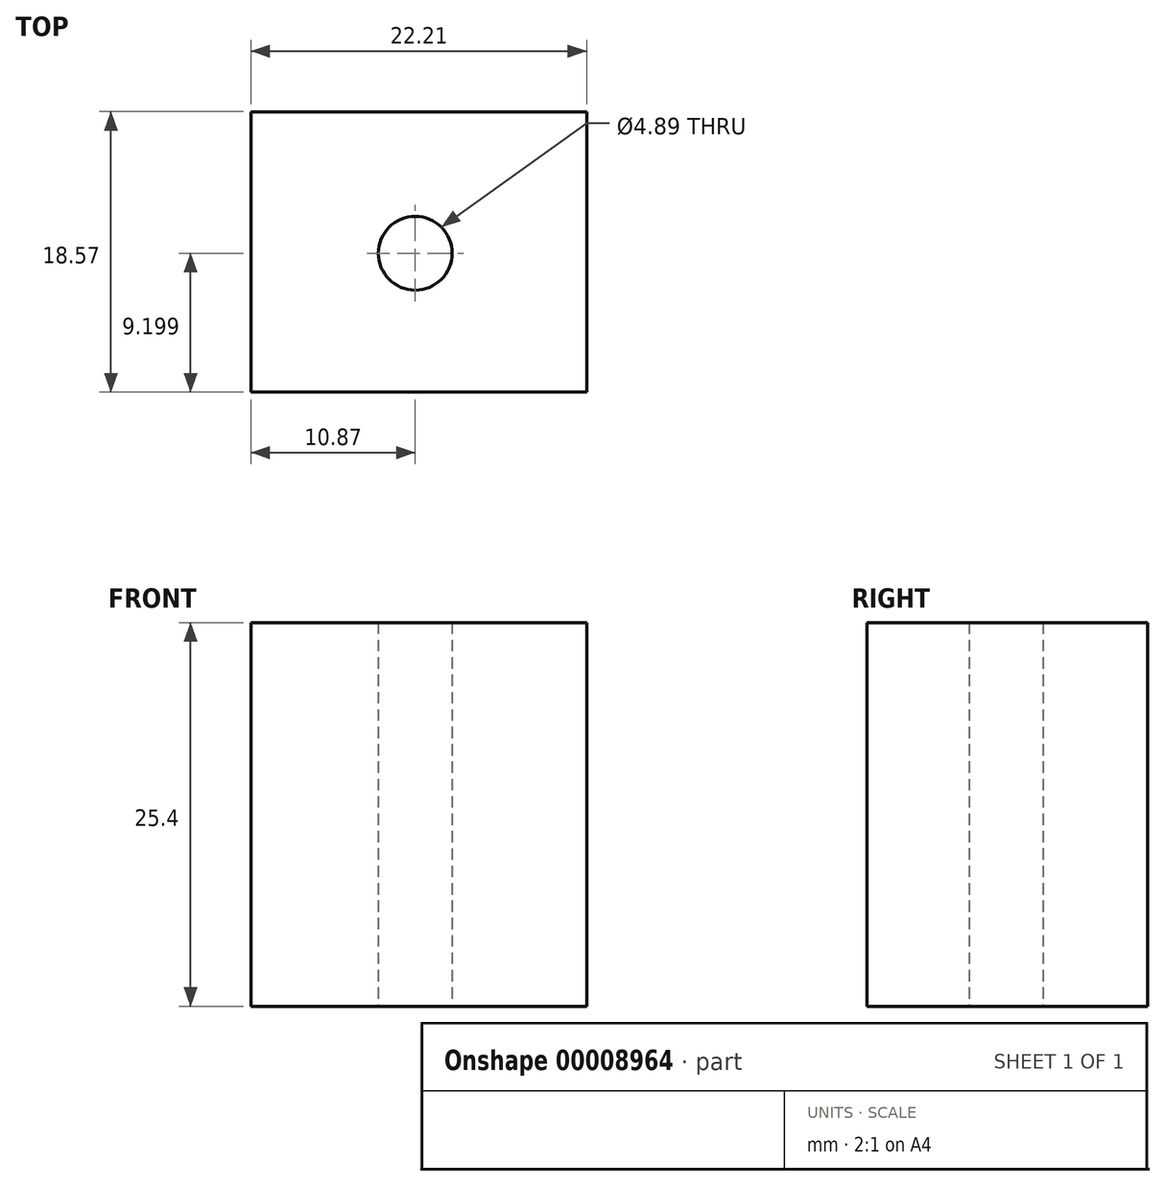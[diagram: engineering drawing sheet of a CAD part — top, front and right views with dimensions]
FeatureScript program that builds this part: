
annotation { "Feature Type Name" : "Feature", "Feature Type Description" : "" }
export const myFeature = defineFeature(function(context is Context, id is Id, definition is map)
    precondition{}
    {
        {
            var Q0;
            Q0=qCreatedBy(makeId("Top.planeOp"),FACE);
            var sketch = newSketch(context, id + "F0", { "sketchPlane" : qUnion([Q0])});
            skLineSegment(sketch, "E0.bottom", {"start": v(-58.65, -30.36) * mm, "end": v(-36.44, -30.36) * mm});
            skLineSegment(sketch, "E0.top", {"start": v(-58.65, -48.93) * mm, "end": v(-36.44, -48.93) * mm});
            skLineSegment(sketch, "E0.left", {"start": v(-58.65, -30.36) * mm, "end": v(-58.65, -48.93) * mm});
            skLineSegment(sketch, "E0.right", {"start": v(-36.44, -30.36) * mm, "end": v(-36.44, -48.93) * mm});
            skSolve(sketch);
        }
        {
            var Q0;
            Q0=makeQuery(id+"F0.imprint","IMPRINT",FACE,{"disambiguationData":[TD([[makeQuery(id+"F0.imprint","IMPRINT",EDGE,{"derivedFrom":sQuery(id+"F0.wireOp",EDGE,"E0.bottom")}),-1.0]])]});
            extrude(context, id + "F1", {"entities" : qUnion([Q0]), "depth" : 25.4 * mm});
        }
        {
            var Q0;
            Q0=qCreatedBy(makeId("Top.planeOp"),FACE);
            var sketch = newSketch(context, id + "F2", { "sketchPlane" : qUnion([Q0])});
            skCircle(sketch, "E1", {"center": v(-47.78, -39.73) * mm, "radius": 2.44 * mm});
            skSolve(sketch);
        }
        {
            var Q0;
            Q0=makeQuery(id+"F2.imprint","IMPRINT",FACE,{"disambiguationData":[TD([[makeQuery(id+"F2.imprint","IMPRINT",EDGE,{"derivedFrom":sQuery(id+"F2.wireOp",EDGE,"E1")}),1.0]])]});
            extrude(context, id + "F3", {"entities" : qUnion([Q0]), "operationType" : NewBodyOperationType.REMOVE, "endBound" : BoundingType.UP_TO_NEXT, "depth" : 25.4 * mm});
        }
    });
